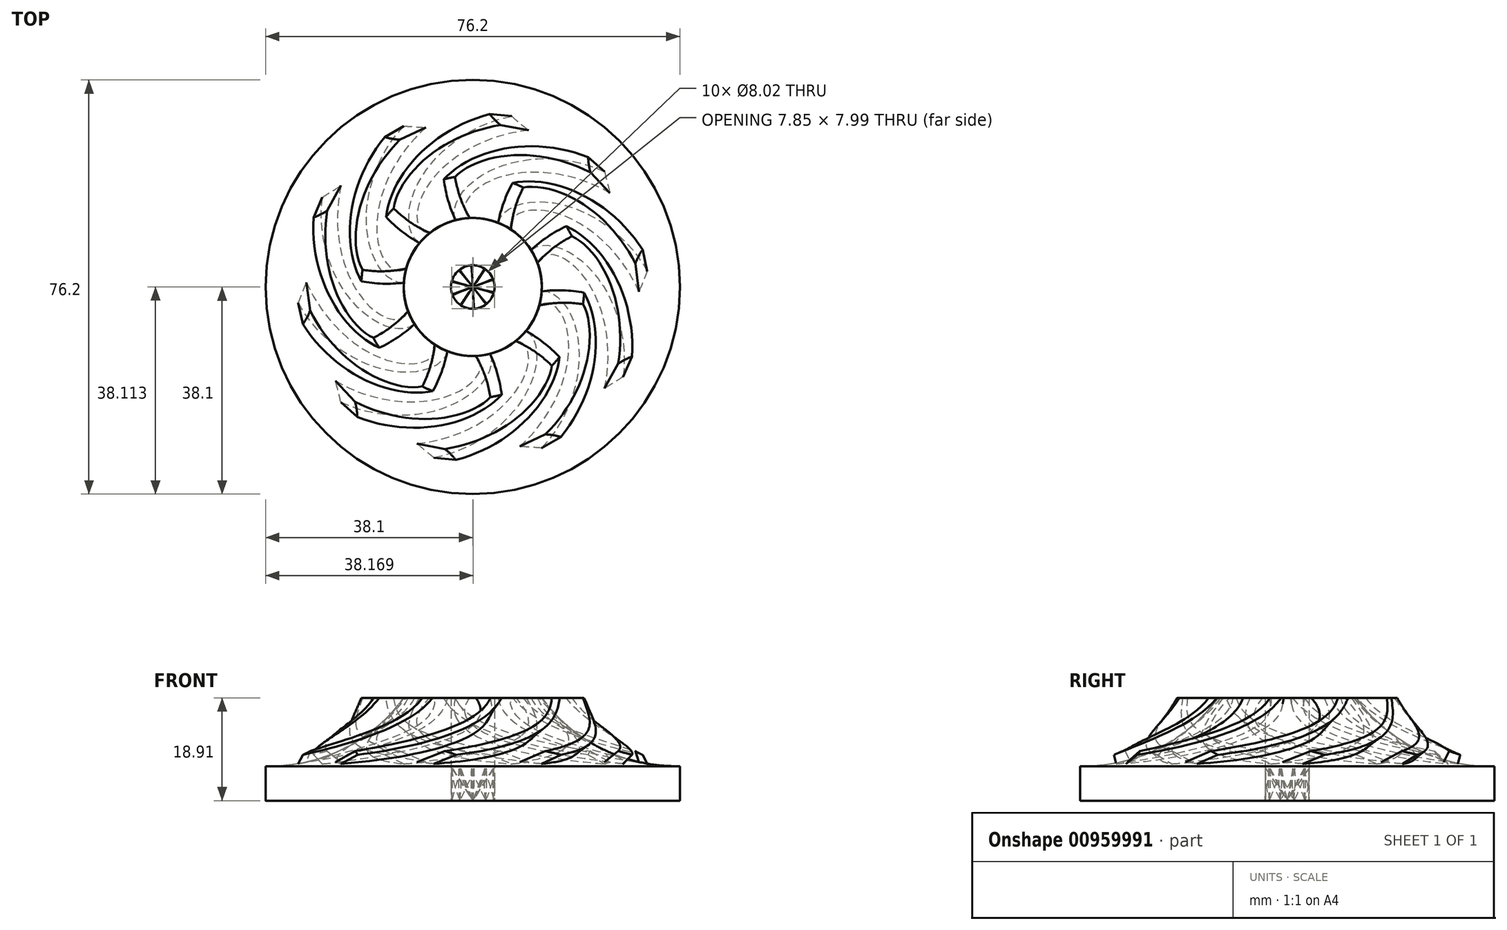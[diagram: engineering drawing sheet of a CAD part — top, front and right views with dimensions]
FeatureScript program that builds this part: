
annotation { "Feature Type Name" : "Feature", "Feature Type Description" : "" }
export const myFeature = defineFeature(function(context is Context, id is Id, definition is map)
    precondition{}
    {
        {
            var Q0;
            Q0=qCreatedBy(makeId("Front.planeOp"),FACE);
            var sketch = newSketch(context, id + "F0", { "sketchPlane" : qUnion([Q0])});
            skLineSegment(sketch, "E0", {"start": v(0, 0) * mm, "end": v(-38.1, 0) * mm});
            skLineSegment(sketch, "E1", {"start": v(-38.1, 0) * mm, "end": v(-38.1, 6.35) * mm});
            skArc(sketch, "E2", {"start": v(-38.1, 6.35) * mm, "mid": v(-23.85, 9.5) * mm, "end": v(-12.7, 18.91) * mm});
            skLineSegment(sketch, "E3", {"start": v(-12.7, 18.91) * mm, "end": v(0, 18.91) * mm});
            skLineSegment(sketch, "E4", {"start": v(0, 18.91) * mm, "end": v(0, 0) * mm});
            skSolve(sketch);
        }
        {
            var Q0;
            Q0=makeQuery(id+"F0.imprint","IMPRINT",FACE,{"disambiguationData":[TD([[makeQuery(id+"F0.imprint","IMPRINT",EDGE,{"derivedFrom":sQuery(id+"F0.wireOp",EDGE,"E0")}),-1.0]])]});
            var Q1;
            Q1=sQuery(id+"F0.wireOp",EDGE,"E4");
            revolve(context, id + "F1", {"surfaceOperationType" : NewSurfaceOperationType.NEW, "entities" : qUnion([Q0]), "axis" : qUnion([Q1]), "revolveType" : RevolveType.FULL});
        }
        {
            var Q0;
            Q0=makeQuery(id+"F1.opRevolve","SWEPT_FACE",FACE,{"disambiguationData":[OSD([sQuery(id+"F0.wireOp",EDGE,"E0")])]});
            var sketch = newSketch(context, id + "F2", { "sketchPlane" : qUnion([Q0])});
            skArc(sketch, "E5", {"start": v(0, 0) * mm, "mid": v(-18.03, 11.2) * mm, "end": v(-37.91, 3.79) * mm});
            skLineSegment(sketch, "E6", {"start": v(0, 0) * mm, "end": v(0, 5.98) * mm});
            skArc(sketch, "E7", {"start": v(0, 5.98) * mm, "mid": v(-17.37, 16.83) * mm, "end": v(-36.73, 10.14) * mm});
            skArc(sketch, "E8", {"start": v(-36.73, 10.14) * mm, "mid": v(-37.45, 6.99) * mm, "end": v(-37.91, 3.79) * mm});
            skSolve(sketch);
        }
        {
            var Q0;
            Q0=makeQuery(id+"F2.imprint","IMPRINT",FACE,{"disambiguationData":[TD([[makeQuery(id+"F2.imprint","IMPRINT",EDGE,{"derivedFrom":sQuery(id+"F2.wireOp",EDGE,"E5")}),-1.0]])]});
            var sketch = newSketch(context, id + "F3", { "sketchPlane" : qUnion([Q0])});
            skCircle(sketch, "E9", {"center": v(0, 0) * mm, "radius": 4 * mm});
            skSolve(sketch);
        }
        {
            var Q0;
            Q0=qSketchRegion(id+"F3",true);
            extrude(context, id + "F4", {"entities" : qUnion([Q0]), "operationType" : NewBodyOperationType.REMOVE, "oppositeDirection" : true, "depth" : 25.4 * mm, "offsetDistance" : 25.4 * mm});
        }
        {
            var Q0;
            Q0=makeQuery(id+"F1.opRevolve","SWEPT_FACE",FACE,{"disambiguationData":[OSD([sQuery(id+"F0.wireOp",EDGE,"E3")])]});
            var sketch = newSketch(context, id + "F5", { "sketchPlane" : qUnion([Q0])});
            skArc(sketch, "E10", {"start": v(-1.96, -41.02) * mm, "mid": v(5.48, -24.46) * mm, "end": v(0, -7.15) * mm});
            skLineSegment(sketch, "E11", {"start": v(0, -7.15) * mm, "end": v(-4.19, -7.15) * mm});
            skArc(sketch, "E12", {"start": v(-4.19, -39.7) * mm, "mid": v(3.49, -23.43) * mm, "end": v(-4.19, -7.15) * mm});
            skArc(sketch, "E13", {"start": v(-1.96, -41.02) * mm, "mid": v(-2.91, -40.08) * mm, "end": v(-4.19, -39.7) * mm});
            skSolve(sketch);
        }
        {
            var Q1;
            {var subQ0=sQuery(id+"F5.wireOp",EDGE,"E13");Q1=makeQuery(id+"F5.imprint","IMPRINT",FACE,{"disambiguationData":[TD([[makeQuery(id+"F5.imprint","IMPRINT",EDGE,{"derivedFrom":subQ0}),-1.0]])]});}
            var Q2;
            Q2=makeQuery(id+"F2.imprint","IMPRINT",FACE,{"disambiguationData":[TD([[makeQuery(id+"F2.imprint","IMPRINT",EDGE,{"derivedFrom":sQuery(id+"F2.wireOp",EDGE,"E5")}),-1.0]])]});
            loft(context, id + "F6", {"operationType" : NewBodyOperationType.ADD, "sheetProfilesArray" : [{ "sheetProfileEntities" : qUnion([Q1]) }, { "sheetProfileEntities" : qUnion([Q2]) }]});
        }
        {
            var Q0;
            Q0=makeQuery(id+"F1.opRevolve","SWEPT_BODY",BODY,{"disambiguationData":[OSD([sQuery(id+"F0.wireOp",EDGE,"E0"),sQuery(id+"F0.wireOp",EDGE,"E1"),sQuery(id+"F0.wireOp",EDGE,"E2"),sQuery(id+"F0.wireOp",EDGE,"E3"),sQuery(id+"F0.wireOp",EDGE,"E4")])]});
            var Q1;
            Q1=makeQuery(id+"F4.boolean.opBoolean","INTERSECT",EDGE,{"derivedFrom":[makeQuery(id+"F1.opRevolve","SWEPT_FACE",FACE,{"disambiguationData":[OSD([sQuery(id+"F0.wireOp",EDGE,"E3")])]}),makeQuery(id+"F4.opExtrude","SWEPT_FACE",FACE,{"disambiguationData":[OSD([sQuery(id+"F3.wireOp",EDGE,"E9")])]})]});
            circularPattern(context, id + "F7", {"entities" : qUnion([Q0]), "axis" : qUnion([Q1]), "angle" : 360 * degree, "instanceCount" : 10, "equalSpace" : true});
        }
        {
            var Q0;
            Q0=qCreatedBy(makeId("Front.planeOp"),FACE);
            var sketch = newSketch(context, id + "F8", { "sketchPlane" : qUnion([Q0])});
            skLineSegment(sketch, "E14", {"start": v(0, 0) * mm, "end": v(-39.52, 0) * mm});
            skLineSegment(sketch, "E15", {"start": v(-39.52, 0) * mm, "end": v(-39.52, 7.44) * mm});
            skArc(sketch, "E16", {"start": v(-39.52, 7.44) * mm, "mid": v(-26.27, 11.52) * mm, "end": v(-19.14, 23.41) * mm});
            skLineSegment(sketch, "E17", {"start": v(-19.14, 23.41) * mm, "end": v(-58.8, 23.41) * mm});
            skLineSegment(sketch, "E18", {"start": v(-58.8, 23.41) * mm, "end": v(-58.8, -12.4) * mm});
            skLineSegment(sketch, "E19", {"start": v(-58.8, -12.4) * mm, "end": v(0, -12.4) * mm});
            skLineSegment(sketch, "E20", {"start": v(0, -12.4) * mm, "end": v(0, 0) * mm});
            skSolve(sketch);
        }
        {
            var Q0;
            Q0=makeQuery(id+"F8.imprint","IMPRINT",FACE,{"disambiguationData":[TD([[makeQuery(id+"F8.imprint","IMPRINT",EDGE,{"derivedFrom":sQuery(id+"F8.wireOp",EDGE,"E14")}),1.0]])]});
            var Q1;
            Q1=sQuery(id+"F8.wireOp",EDGE,"E20");
            revolve(context, id + "F9", {"operationType" : NewBodyOperationType.REMOVE, "surfaceOperationType" : NewSurfaceOperationType.NEW, "entities" : qUnion([Q0]), "axis" : qUnion([Q1]), "revolveType" : RevolveType.FULL, "oppositeDirection" : true});
        }
    });
